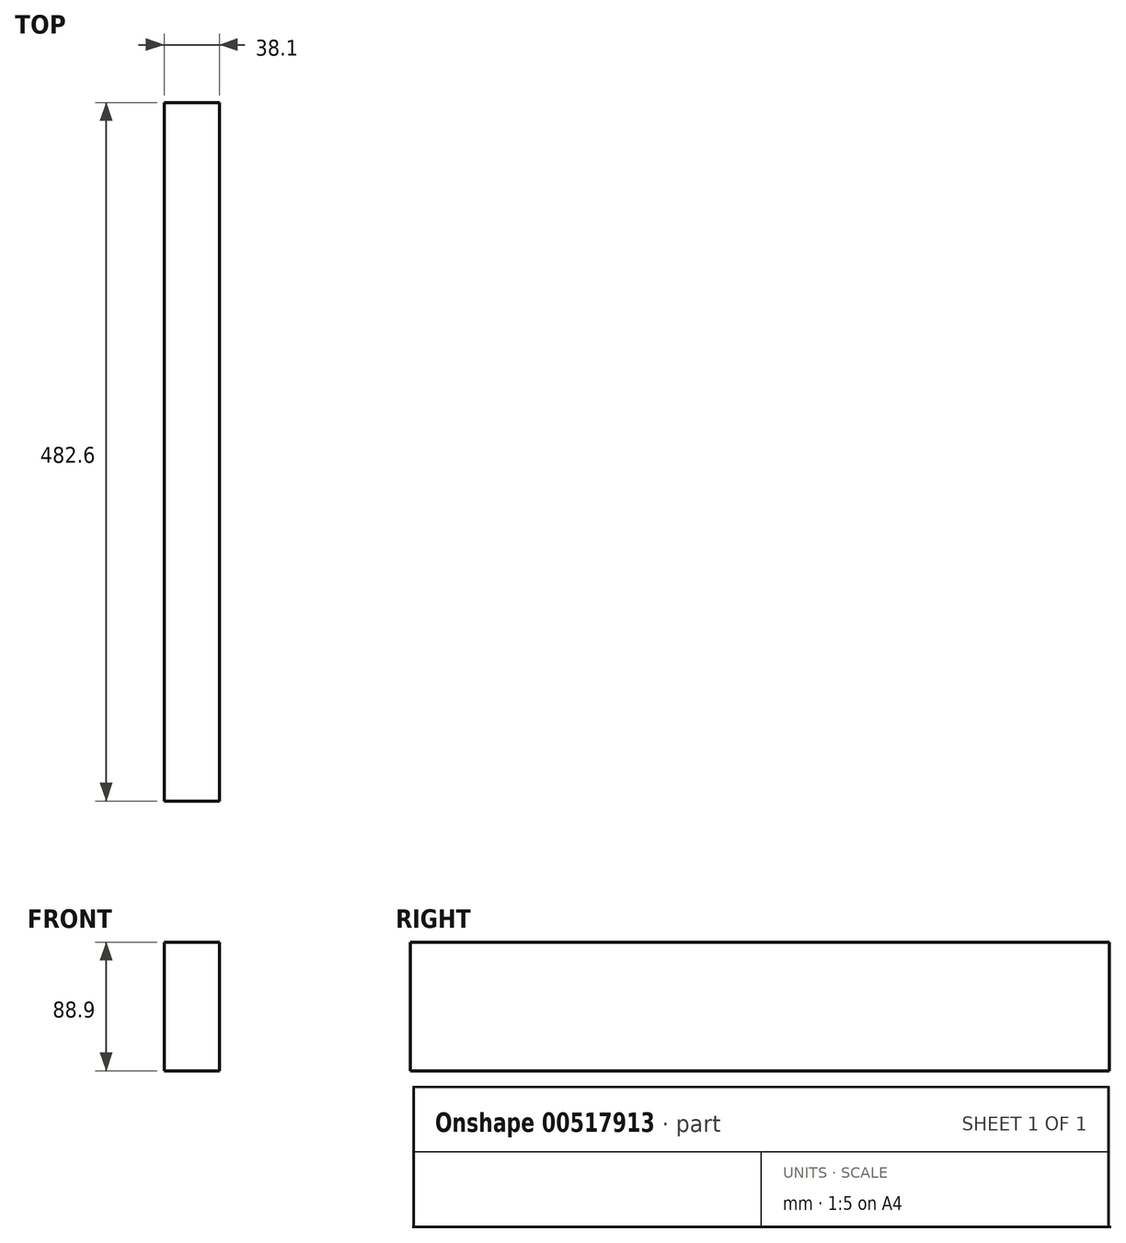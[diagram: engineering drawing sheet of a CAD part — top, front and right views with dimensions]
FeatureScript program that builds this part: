
annotation { "Feature Type Name" : "Feature", "Feature Type Description" : "" }
export const myFeature = defineFeature(function(context is Context, id is Id, definition is map)
    precondition{}
    {
        {
            var Q0;
            Q0=qCreatedBy(makeId("Front.planeOp"),FACE);
            var sketch = newSketch(context, id + "F0", { "sketchPlane" : qUnion([Q0])});
            skLineSegment(sketch, "E0.bottom", {"start": v(19.05, 44.45) * mm, "end": v(-19.05, 44.45) * mm});
            skLineSegment(sketch, "E0.top", {"start": v(19.05, -44.45) * mm, "end": v(-19.05, -44.45) * mm});
            skLineSegment(sketch, "E0.left", {"start": v(19.05, 44.45) * mm, "end": v(19.05, -44.45) * mm});
            skLineSegment(sketch, "E0.right", {"start": v(-19.05, 44.45) * mm, "end": v(-19.05, -44.45) * mm});
            skPoint(sketch, "E0.middle", {"position": v(0, 0) * mm});
            skSolve(sketch);
        }
        {
            var Q0;
            Q0=makeQuery(id+"F0.imprint","IMPRINT",FACE,{"disambiguationData":[TD([[makeQuery(id+"F0.imprint","IMPRINT",EDGE,{"derivedFrom":sQuery(id+"F0.wireOp",EDGE,"E0.bottom")}),1.0]])]});
            extrude(context, id + "F1", {"entities" : qUnion([Q0]), "endBound" : BoundingType.SYMMETRIC, "depth" : 482.6 * mm, "offsetDistance" : 25.4 * mm});
        }
    });
